# Revit family: Drinking_Fountain-Oasis-Barrier-Free_Versacooler_II_with_Filtration_System-PGF8AC
name_source: partatom
category: Plumbing Fixtures
revit_build: Autodesk Revit MEP 2013 (Build: 20130531_2115(x64)
units: mm (PartAtom-declared; Revit-internal decimal feet)

## types (4) — shared parameters
Apparent Load = 500 VA
Base = Metal - Oasis International - Steel Painted Sandstone - Exterior Finish
Compression HP = 0 VA
Connection Note = Water inlet and outlet location can be adjusted. Contact Oasis for more information.
Default Elevation = 2' - 3"
Description = Barrier-Free Versacooler II W/Filtration System
Full Load Amps = 4 A
Manufacturer = Oasis International
Manufacturer Fax Number = (614)322-4557
Number of Poles = 1
Power Factor = 1
Product Documentation Link = http://www.oasiscoolers.com
Product Page URL = http://www.oasiscoolers.com
Rated Watts = 500 W
Top = Metal - Oasis International - Brushed Stainless Steel - Exterior Finish
URL = http://www.oasiscoolers.com
Voltage = 115 V

## per-type parameters (varying)
| type | Base Rate | Chiller | Pre Cooler | Product Name | Rated Capacity |
| PGF8AC | 8 GPM | Yes | No | Filtered Versacooler II | 8 GPM |
| PGFAC | 0 GPM | No |  | Non Refrigerated, Filtered Versacooler II | 0 GPM |
| PGFAC CSTN | 0 GPM | No |  | Non Refrigerated, Filtered, Copper Versacooler II | 0 GPM |
| PGF8AC CSTN | 0 GPM | Yes |  | Filtered, Copper Versacooler II | 0 GPM |

note: column(s) folded — value = type name in every type: Model

## geometry (parser evidence)
native form markers: Blend x6, Sweep x20
no freeform markers — native parametric forms only
